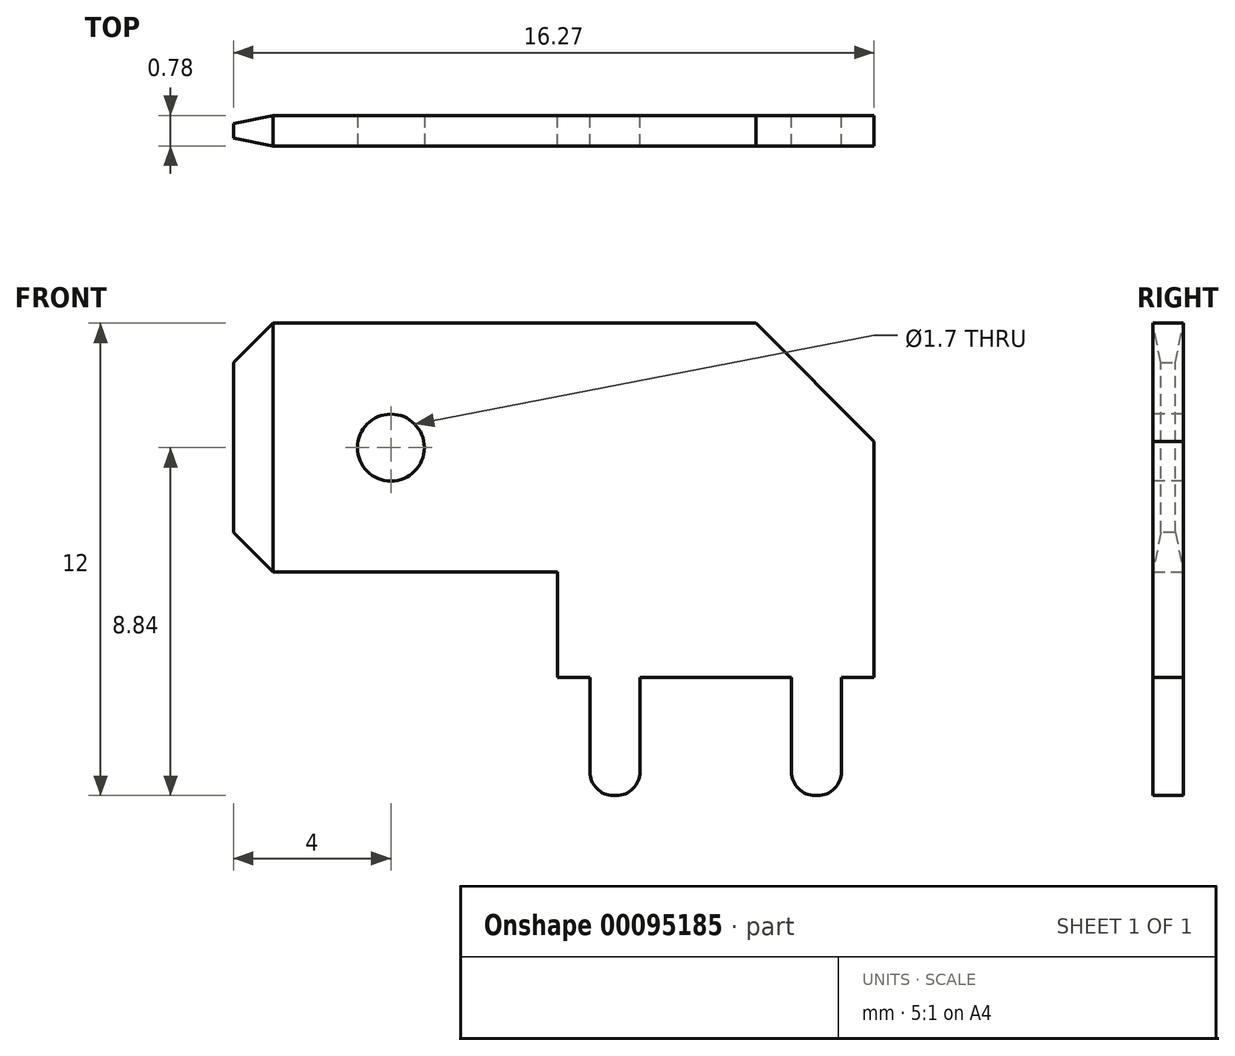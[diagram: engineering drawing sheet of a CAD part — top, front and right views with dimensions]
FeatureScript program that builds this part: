
annotation { "Feature Type Name" : "Feature", "Feature Type Description" : "" }
export const myFeature = defineFeature(function(context is Context, id is Id, definition is map)
    precondition{}
    {
        {
            var Q0;
            Q0=qCreatedBy(makeId("Front.planeOp"),FACE);
            var sketch = newSketch(context, id + "F0", { "sketchPlane" : qUnion([Q0])});
            skLineSegment(sketch, "E0", {"start": v(-4.02, 0) * mm, "end": v(-3.2, 0) * mm});
            skLineSegment(sketch, "E1", {"start": v(4.02, 0) * mm, "end": v(4.02, 6) * mm});
            skLineSegment(sketch, "E2", {"start": v(4.02, 6) * mm, "end": v(1.02, 9) * mm});
            skLineSegment(sketch, "E3", {"start": v(1.02, 9) * mm, "end": v(-11.25, 9) * mm});
            skLineSegment(sketch, "E4", {"start": v(-12.25, 9) * mm, "end": v(-12.25, 2.68) * mm});
            skLineSegment(sketch, "E5", {"start": v(-11.25, 2.68) * mm, "end": v(-4.02, 2.68) * mm});
            skLineSegment(sketch, "E6", {"start": v(-4.02, 2.68) * mm, "end": v(-4.02, 0) * mm});
            skLineSegment(sketch, "E7.top", {"start": v(-2.6, -3) * mm, "end": v(-2.53, -3) * mm});
            skLineSegment(sketch, "E7.left", {"start": v(-3.2, 0) * mm, "end": v(-3.2, -2.4) * mm});
            skLineSegment(sketch, "E7.right", {"start": v(-1.93, 0) * mm, "end": v(-1.93, -2.4) * mm});
            skLineSegment(sketch, "E8.top", {"start": v(2.6, -3) * mm, "end": v(2.53, -3) * mm});
            skLineSegment(sketch, "E8.left", {"start": v(3.2, 0) * mm, "end": v(3.2, -2.4) * mm});
            skLineSegment(sketch, "E8.right", {"start": v(1.92, 0) * mm, "end": v(1.92, -2.4) * mm});
            skLineSegment(sketch, "E9", {"start": v(-1.92, 0) * mm, "end": v(1.92, 0) * mm, "construction": true});
            skPoint(sketch, "E10.visualSharp", {"position": v(-12.25, 2.68) * mm});
            skPoint(sketch, "E11.visualSharp", {"position": v(-12.25, 9) * mm});
            skPoint(sketch, "E12.visualSharp", {"position": v(-3.2, -3) * mm});
            skArc(sketch, "E12.filletArc", {"start": v(-3.2, -2.4) * mm, "mid": v(-3.02, -2.82) * mm, "end": v(-2.6, -3) * mm});
            skPoint(sketch, "E13.visualSharp", {"position": v(-1.93, -3) * mm});
            skArc(sketch, "E13.filletArc", {"start": v(-2.53, -3) * mm, "mid": v(-2.1, -2.82) * mm, "end": v(-1.93, -2.4) * mm});
            skPoint(sketch, "E14.visualSharp", {"position": v(1.93, -3) * mm});
            skArc(sketch, "E14.filletArc", {"start": v(1.93, -2.4) * mm, "mid": v(2.1, -2.82) * mm, "end": v(2.53, -3) * mm});
            skPoint(sketch, "E15.visualSharp", {"position": v(3.2, -3) * mm});
            skArc(sketch, "E15.filletArc", {"start": v(2.6, -3) * mm, "mid": v(3.02, -2.82) * mm, "end": v(3.2, -2.4) * mm});
            skLineSegment(sketch, "E16", {"start": v(-11.25, 2.68) * mm, "end": v(-12.25, 2.68) * mm});
            skLineSegment(sketch, "E17", {"start": v(-12.25, 9) * mm, "end": v(-11.25, 9) * mm});
            skLineSegment(sketch, "E18", {"start": v(-11.25, 9) * mm, "end": v(-11.25, 2.68) * mm, "construction": true});
            skLineSegment(sketch, "E19.trimOffspring", {"start": v(3.2, 0) * mm, "end": v(4.02, 0) * mm});
            skLineSegment(sketch, "E20.trimOffspring", {"start": v(-1.92, 0) * mm, "end": v(1.92, 0) * mm});
            skSolve(sketch);
        }
        {
            var Q0;
            Q0 = qSketchRegion(id + "F0", true);
            extrude(context, id + "F1", {"entities" : qUnion([Q0]), "endBound" : BoundingType.SYMMETRIC, "depth" : 0.77 * mm});
        }
        {
            var Q0;
            Q0=makeQuery(id+"F1.opExtrude","SWEPT_EDGE",EDGE,{"disambiguationData":[OSD([sQuery(id+"F0.wireOp",EDGE,"E4"),sQuery(id+"F0.wireOp",EDGE,"E17")])]});
            var Q1;
            Q1=makeQuery(id+"F1.opExtrude","SWEPT_EDGE",EDGE,{"disambiguationData":[OSD([sQuery(id+"F0.wireOp",EDGE,"E4"),sQuery(id+"F0.wireOp",EDGE,"E16")])]});
            chamfer(context, id + "F2", {"entities" : qUnion([Q0, Q1]), "width" : 1 * mm, "tangentPropagation" : true});
        }
        {
            var Q0;
            Q0=makeQuery(id+"F1.opExtrude","CAP_FACE",FACE,{"disambiguationData":[OSD([sQuery(id+"F0.wireOp",EDGE,"E0"),sQuery(id+"F0.wireOp",EDGE,"E1"),sQuery(id+"F0.wireOp",EDGE,"E2"),sQuery(id+"F0.wireOp",EDGE,"E3"),sQuery(id+"F0.wireOp",EDGE,"E4"),sQuery(id+"F0.wireOp",EDGE,"E5"),sQuery(id+"F0.wireOp",EDGE,"E6"),sQuery(id+"F0.wireOp",EDGE,"E7.top"),sQuery(id+"F0.wireOp",EDGE,"E7.left"),sQuery(id+"F0.wireOp",EDGE,"E7.right"),sQuery(id+"F0.wireOp",EDGE,"E8.top"),sQuery(id+"F0.wireOp",EDGE,"E8.left"),sQuery(id+"F0.wireOp",EDGE,"E8.right"),sQuery(id+"F0.wireOp",EDGE,"E10.filletArc"),sQuery(id+"F0.wireOp",EDGE,"E11.filletArc"),sQuery(id+"F0.wireOp",EDGE,"E12.filletArc"),sQuery(id+"F0.wireOp",EDGE,"E13.filletArc"),sQuery(id+"F0.wireOp",EDGE,"E14.filletArc"),sQuery(id+"F0.wireOp",EDGE,"E15.filletArc")])],"isStart":false});
            var sketch = newSketch(context, id + "F3", { "sketchPlane" : qUnion([Q0])});
            skLineSegment(sketch, "E21", {"start": v(-12.25, 5.84) * mm, "end": v(4.02, 5.84) * mm, "construction": true});
            skCircle(sketch, "E22", {"center": v(-8.25, 5.84) * mm, "radius": 0.85 * mm});
            skSolve(sketch);
        }
        {
            var Q0;
            Q0 = qSketchRegion(id + "F3", true);
            extrude(context, id + "F4", {"entities" : qUnion([Q0]), "operationType" : NewBodyOperationType.REMOVE, "endBound" : BoundingType.THROUGH_ALL, "oppositeDirection" : true, "depth" : 25 * mm});
        }
        {
            var Q0;
            Q0=makeQuery(id+"F1.opExtrude","SWEPT_FACE",FACE,{"disambiguationData":[OSD([sQuery(id+"F0.wireOp",EDGE,"E3")])]});
            var sketch = newSketch(context, id + "F5", { "sketchPlane" : qUnion([Q0])});
            skLineSegment(sketch, "E23", {"start": v(-11.25, 0.38) * mm, "end": v(-12.25, 0.18) * mm});
            skLineSegment(sketch, "E24", {"start": v(-12.25, 0.19) * mm, "end": v(-12.25, 0.39) * mm});
            skLineSegment(sketch, "E25", {"start": v(-12.25, 0) * mm, "end": v(1.02, 0) * mm, "construction": true});
            skLineSegment(sketch, "E26", {"start": v(-11.25, 0.38) * mm, "end": v(-12.25, 0.39) * mm});
            skLineSegment(sketch, "E27.MirrorCS", {"start": v(-11.25, -0.38) * mm, "end": v(-12.25, -0.18) * mm});
            skLineSegment(sketch, "E28.MirrorCS", {"start": v(-12.25, -0.19) * mm, "end": v(-12.25, -0.39) * mm});
            skLineSegment(sketch, "E29.MirrorCS", {"start": v(-11.25, -0.38) * mm, "end": v(-12.25, -0.39) * mm});
            skLineSegment(sketch, "E30.0", {"start": v(-12.25, -0.39) * mm, "end": v(-12.25, 0.39) * mm, "construction": true});
            skSolve(sketch);
        }
        {
            var Q0;
            Q0 = qSketchRegion(id + "F5", true);
            extrude(context, id + "F6", {"entities" : qUnion([Q0]), "operationType" : NewBodyOperationType.REMOVE, "endBound" : BoundingType.THROUGH_ALL, "oppositeDirection" : true, "depth" : 25 * mm});
        }
    });
